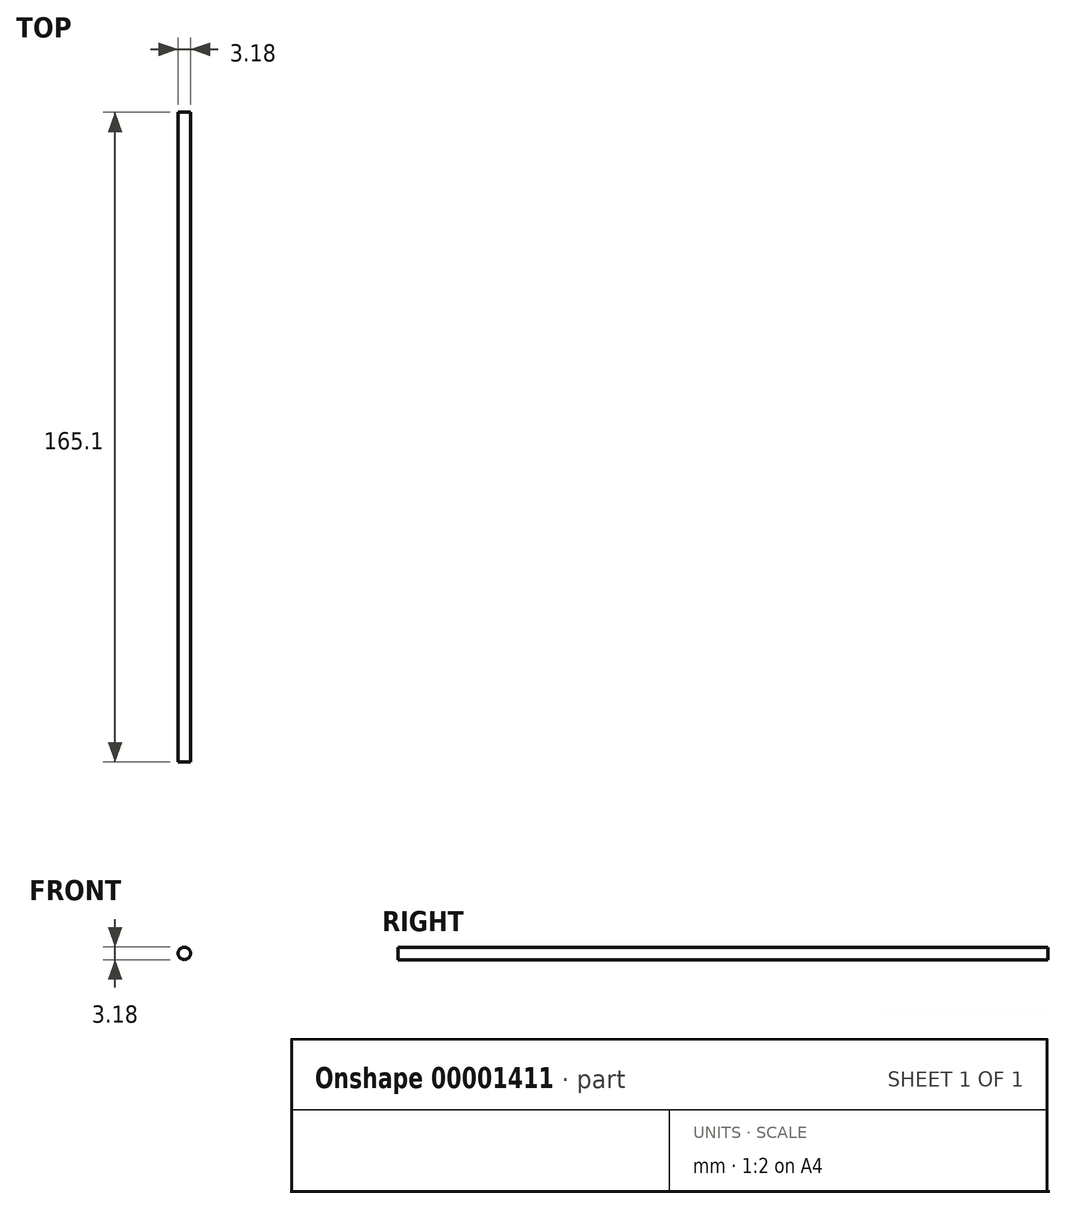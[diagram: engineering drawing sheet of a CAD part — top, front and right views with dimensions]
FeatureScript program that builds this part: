
annotation { "Feature Type Name" : "Feature", "Feature Type Description" : "" }
export const myFeature = defineFeature(function(context is Context, id is Id, definition is map)
    precondition{}
    {
        {
            var Q0;
            Q0=qCreatedBy(makeId("Front.planeOp"),FACE);
            var sketch = newSketch(context, id + "F0", { "sketchPlane" : qUnion([Q0])});
            skCircle(sketch, "E0", {"center": v(0, 0) * mm, "radius": 1.59 * mm});
            skSolve(sketch);
        }
        {
            var Q0;
            Q0 = qSketchRegion(id + "F0", true);
            extrude(context, id + "F1", {"entities" : qUnion([Q0]), "endBound" : BoundingType.SYMMETRIC, "depth" : 165.1 * mm});
        }
    });
